# Revit family: TowelHolder-WithSelf-Vitra-EternitySeries-A44879
name_source: partatom
category: Plumbing Fixtures
revit_build: Autodesk Revit 2017 (Build: 20160225_1515(x64)
units: mm (PartAtom-declared; Revit-internal decimal feet)

## family parameters
Cut with Voids When Loaded = No
Host = Face
OmniClass Number = 23.45.05.14.99
OmniClass Title = Other Sanitary Washing Plumbing Fixtures
Part Type = Normal
Room Calculation Point = No
Round Connector Dimension = Use Diameter
Shared = Yes

## types (2) — shared parameters
BIMobject category = Sanitary - Bathroom Accessories
CW Connection = No
Default Elevation = 2200 mm
Depth(mm) = 140 mm
Description = Eternity Towel Holder with self
Design country = Turkey
First Material = Vitra-Wood
HW Connection = No
Height(mm) = 48 mm  [stored 0.15748 ft]
IFC Classification = Sanitary Terminal
Manufacturer = Vitra
Manufacturer name = Vitra
MountingType = Wall-mounted
NBS Referans Code = 35-75-90
NBS Referans Description = Towel Rails
Nominal height = 0.000
Nominal width = 0.000
OmniClass Code = 23-31 25 25
OmniClass Description = Towel Bars
Product Type = Built-in Towel Holder with Self
Product certification = https://vitraglobal.com
Product data url = https://www.vitraglobal.com
Product family = EternitySeries
Product group = Towel Holder with Self
Technical description = https://www.vitra.com.tr
UNSPSC Code = 56
UNSPSC Description = Furniture and Furnishings
URL = https://vitraglobal.com
Uniclass 1.4 Code = L8245
Uniclass 1.4 Description = Towel rails
Uniclass 2.0 Code = PR-35-75-90
Uniclass 2.0 Description = Towel Rails
Uniclass 2015 Code = Pr_40_20_76_90
Uniclass 2015 Name = Towel rails
Uniformat II Code = E2010
Uniformat II Description = FURNISHINGS
Vent Connection = No
Warranty Period (Year) = 5 years
Waste Connection = No
Weight Net (kg) = 1,720
Width(mm) = 660 mm
Youtube = https://www.youtube.com
zero-valued in all types: CWFU, Cost, HWFU, WFU

## per-type parameters (varying)
| type | Article No. (default) | Coating Material | Color | Model | Product SKU |
| TowelHolder-WithSelf-Vitra-EternitySeries(Chrome)-A44879 | A44879 | Vitra-Chrome | Chrome | A44879 | A44879 |
| TowelHolder-WithSelf-Vitra-EternitySeries(Gold)-A4487923 | A4487923 | Vitra-Gold | Gold | A4487923 | A4487923 |

note: [stored X ft] marks values corroborated as IEEE doubles in the binary element streams (Revit-internal decimal feet)

## geometry (parser evidence)
native form markers: Sweep x3
no freeform markers — native parametric forms only
